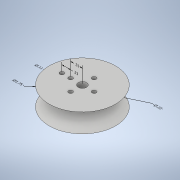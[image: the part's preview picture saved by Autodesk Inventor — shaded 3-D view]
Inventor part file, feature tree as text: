
AUTODESK INVENTOR PART (.ipt)
format: ipt  version: 2020 (Build 240168000, 168)  size: 174,080 bytes
history: native  units: in
note: dims shown in document units (in); Inventor stores cm internally (conversion verified against a paired STEP export)
features: extrude x4, sketch x4, chamfer x2
ambient origin geometry x8: Origin, YZ Plane, XZ Plane, XY Plane, X Axis, Y Axis, Z Axis, Center Point
bodies: Solid1 (feature_tree)
feature tree (10):
  extrude  "Extrusion1"  Depth=0.25in TaperAngle=0.0deg
  chamfer  "Chamfer1"  Distance=0.5in Angle=45.0deg
  extrude  "Extrusion2"  Depth=0.5in TaperAngle=45.0deg
  chamfer  "Chamfer2"  Distance=0.23in
  extrude  "Extrusion3"  Depth=0.2in
  extrude  "Extrusion4"  Depth=0.2in
  sketch  "Sketch1"  dims[d0=1.75in d1=0.25in d2=0.0in d7=0.5in d8=0.25in d9=45.0deg]
  sketch  "Sketch2"  dims[d10=0.25in d11=0.0in d12=0.5in d13=0.25in d14=45.0deg]
  sketch  "Sketch4"  dims[d28=0.22in]
  sketch  "Sketch5"  dims[d29=0.31in d30=0.23in d31=0.31in d32=0.31in d33=0.31in d34=0.11in d35=0.11in d36=0.11in d37=0.11in d38=0.11in d39=0.6in d40=0.0in d57=1.75in d58=0.875in d59=0.2in d60=0.0in d26=1.5792in d27=1.75in d41=0.3293in d42=1.75in d43=1.4463in d44=0.1321in d45=0.0594in d46=0.22in d47=0.0541in d48=0.0954in d49=0.31in d50=0.0598in d51=0.0586in d52=0.23in d53=-0.3764in d54=0.0667in d55=0.0375in d56=0.11in]
